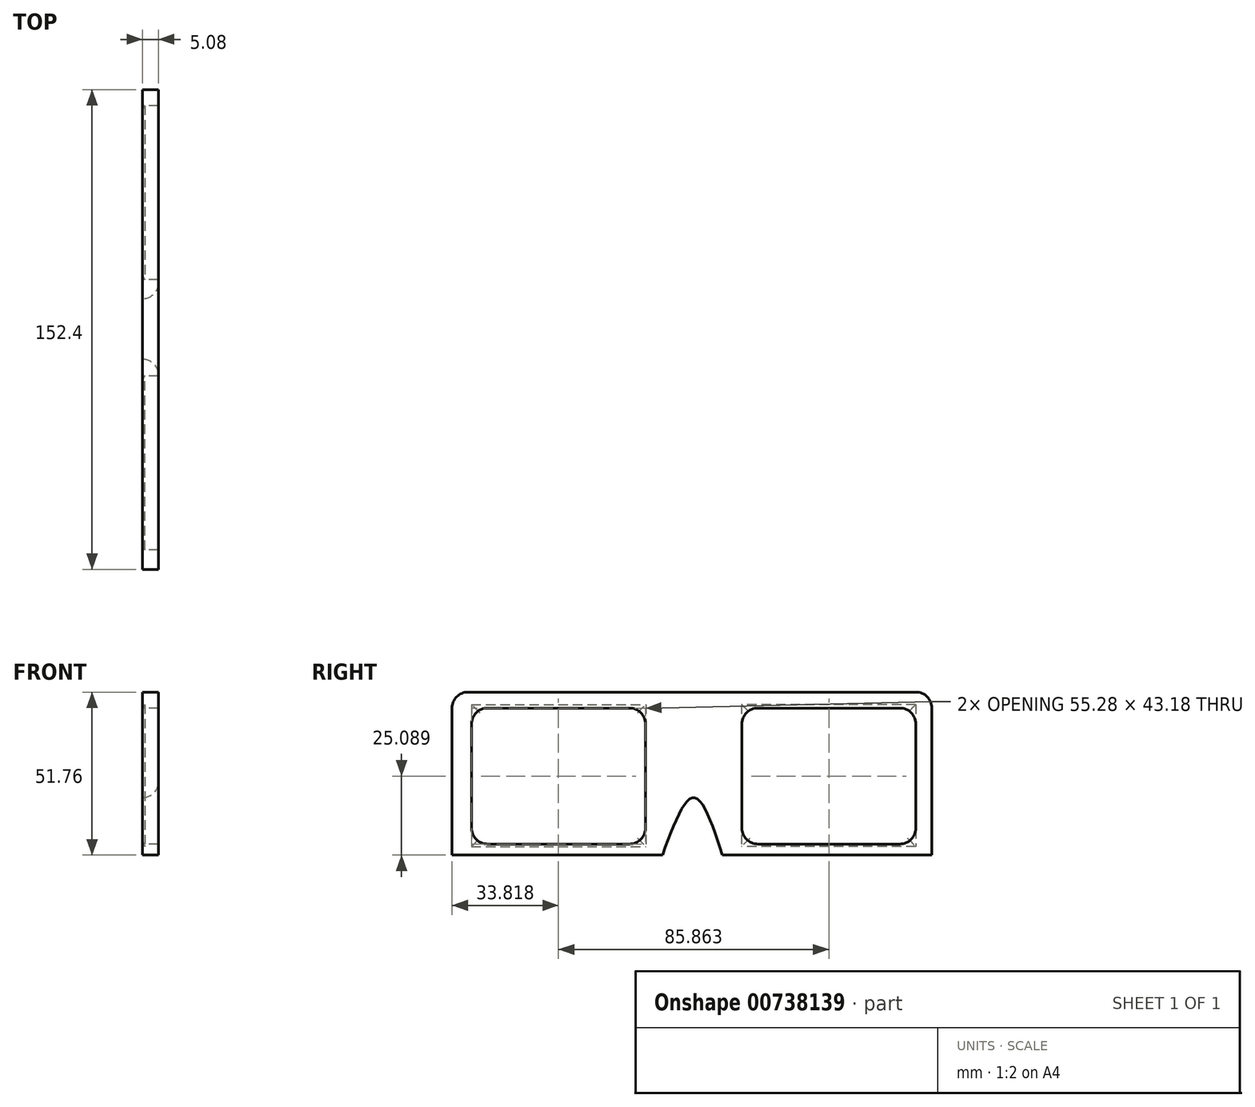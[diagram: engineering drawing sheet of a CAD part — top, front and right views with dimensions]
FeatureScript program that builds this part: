
annotation { "Feature Type Name" : "Feature", "Feature Type Description" : "" }
export const myFeature = defineFeature(function(context is Context, id is Id, definition is map)
    precondition{}
    {
        {
            var Q0;
            Q0=qCreatedBy(makeId("Right.planeOp"),FACE);
            var sketch = newSketch(context, id + "F0", { "sketchPlane" : qUnion([Q0])});
            skLineSegment(sketch, "E0.bottom", {"start": v(-76.75, 40.78) * mm, "end": v(75.65, 40.78) * mm});
            skLineSegment(sketch, "E0.top", {"start": v(-76.75, -22.72) * mm, "end": v(75.65, -22.72) * mm});
            skLineSegment(sketch, "E0.left", {"start": v(-76.75, 40.78) * mm, "end": v(-76.75, -22.72) * mm});
            skLineSegment(sketch, "E0.right", {"start": v(75.65, 40.78) * mm, "end": v(75.65, -22.72) * mm});
            skSolve(sketch);
        }
        {
            var Q0;
            Q0 = qSketchRegion(id + "F0", true);
            extrude(context, id + "F1", {"entities" : qUnion([Q0]), "depth" : 5.08 * mm, "offsetDistance" : 25.4 * mm});
        }
        {
            var Q0;
            Q0=makeQuery(id+"F1.opExtrude","SWEPT_EDGE",EDGE,{"disambiguationData":[OSD([sQuery(id+"F0.wireOp",EDGE,"E0.bottom"),sQuery(id+"F0.wireOp",EDGE,"E0.left")])]});
            var Q1;
            Q1=makeQuery(id+"F1.opExtrude","SWEPT_EDGE",EDGE,{"disambiguationData":[OSD([sQuery(id+"F0.wireOp",EDGE,"E0.top"),sQuery(id+"F0.wireOp",EDGE,"E0.left")])]});
            var Q2;
            Q2=makeQuery(id+"F1.opExtrude","SWEPT_EDGE",EDGE,{"disambiguationData":[OSD([sQuery(id+"F0.wireOp",EDGE,"E0.top"),sQuery(id+"F0.wireOp",EDGE,"E0.right")])]});
            var Q3;
            Q3=makeQuery(id+"F1.opExtrude","SWEPT_EDGE",EDGE,{"disambiguationData":[OSD([sQuery(id+"F0.wireOp",EDGE,"E0.bottom"),sQuery(id+"F0.wireOp",EDGE,"E0.right")])]});
            fillet(context, id + "F2", {"entities" : qUnion([Q0, Q1, Q2, Q3]), "radius" : 5.08 * mm, "tangentPropagation" : true, "allowEdgeOverflow" : false});
        }
        {
            var Q0;
            Q0=makeQuery(id+"F1.opExtrude","CAP_FACE",FACE,{"disambiguationData":[OSD([sQuery(id+"F0.wireOp",EDGE,"E0.bottom"),sQuery(id+"F0.wireOp",EDGE,"E0.top"),sQuery(id+"F0.wireOp",EDGE,"E0.left"),sQuery(id+"F0.wireOp",EDGE,"E0.right")])],"isStart":true});
            var sketch = newSketch(context, id + "F3", { "sketchPlane" : qUnion([Q0])});
            skLineSegment(sketch, "E1.bottom", {"start": v(-70.57, 35.7) * mm, "end": v(-15.3, 35.7) * mm});
            skLineSegment(sketch, "E1.top", {"start": v(-70.57, -7.48) * mm, "end": v(-15.3, -7.48) * mm});
            skLineSegment(sketch, "E1.left", {"start": v(-70.57, 35.7) * mm, "end": v(-70.57, -7.48) * mm});
            skLineSegment(sketch, "E1.right", {"start": v(-15.3, 35.7) * mm, "end": v(-15.3, -7.48) * mm});
            skLineSegment(sketch, "E2.MirrorCS", {"start": v(70.57, -7.48) * mm, "end": v(15.3, -7.48) * mm});
            skLineSegment(sketch, "E3.MirrorCS", {"start": v(70.57, 35.7) * mm, "end": v(70.57, -7.48) * mm});
            skLineSegment(sketch, "E4.MirrorCS", {"start": v(15.3, 35.7) * mm, "end": v(15.3, -7.48) * mm});
            skLineSegment(sketch, "E5.MirrorCS", {"start": v(70.57, 35.7) * mm, "end": v(15.3, 35.7) * mm});
            skLineSegment(sketch, "E6", {"start": v(-75.65, -10.98) * mm, "end": v(76.75, -10.98) * mm});
            skLineSegment(sketch, "E7", {"start": v(76.75, -10.98) * mm, "end": v(76.75, -28.42) * mm});
            skLineSegment(sketch, "E8", {"start": v(76.75, -28.42) * mm, "end": v(-75.65, -28.42) * mm});
            skLineSegment(sketch, "E9", {"start": v(-75.65, -28.42) * mm, "end": v(-75.65, -10.98) * mm});
            skFitSpline(sketch, "E10", {"points": [v(-9.1, -10.98) * mm, v(0, 7.25) * mm, v(9.9, -10.98) * mm], "startDerivative": vector(17.93, 54.77) * mm, "endDerivative": vector(20.06, -54.6) * mm});
            skSolve(sketch);
        }
        {
            var Q0;
            Q0 = qSketchRegion(id + "F3", true);
            extrude(context, id + "F4", {"entities" : qUnion([Q0]), "operationType" : NewBodyOperationType.REMOVE, "oppositeDirection" : true, "depth" : 25.4 * mm, "offsetDistance" : 25.4 * mm});
        }
        {
            var Q0;
            Q0=makeQuery(id+"F4.boolean.opBoolean","COPY",EDGE,{"derivedFrom":makeQuery(id+"F4.opExtrude","SWEPT_EDGE",EDGE,{"disambiguationData":[OSD([sQuery(id+"F0.wireOp",EDGE,"E0.right"),sQuery(id+"F3.wireOp",EDGE,"E6"),sQuery(id+"F3.wireOp",EDGE,"E9")])]})});
            var Q1;
            Q1=makeQuery(id+"F4.boolean.opBoolean","COPY",EDGE,{"derivedFrom":makeQuery(id+"F4.opExtrude","CAP_EDGE",EDGE,{"disambiguationData":[OSD([sQuery(id+"F3.wireOp",EDGE,"E10")])],"isStart":true})});
            var Q2;
            Q2=makeQuery(id+"F4.boolean.opBoolean","INTERSECT",EDGE,{"derivedFrom":[makeQuery(id+"F1.opExtrude","CAP_FACE",FACE,{"disambiguationData":[OSD([sQuery(id+"F0.wireOp",EDGE,"E0.bottom"),sQuery(id+"F0.wireOp",EDGE,"E0.top"),sQuery(id+"F0.wireOp",EDGE,"E0.left"),sQuery(id+"F0.wireOp",EDGE,"E0.right")])],"isStart":false}),makeQuery(id+"F4.opExtrude","SWEPT_FACE",FACE,{"disambiguationData":[OSD([sQuery(id+"F3.wireOp",EDGE,"E10")])]})]});
            var Q3;
            Q3=makeQuery(id+"F4.boolean.opBoolean","COPY",EDGE,{"derivedFrom":makeQuery(id+"F4.opExtrude","SWEPT_EDGE",EDGE,{"disambiguationData":[OSD([sQuery(id+"F0.wireOp",EDGE,"E0.left"),sQuery(id+"F3.wireOp",EDGE,"E6"),sQuery(id+"F3.wireOp",EDGE,"E7")])]})});
            var Q4;
            Q4=makeQuery(id+"F4.boolean.opBoolean","COPY",EDGE,{"derivedFrom":makeQuery(id+"F4.opExtrude","SWEPT_EDGE",EDGE,{"disambiguationData":[OSD([sQuery(id+"F3.wireOp",EDGE,"E3.MirrorCS"),sQuery(id+"F3.wireOp",EDGE,"E5.MirrorCS")])]})});
            var Q5;
            Q5=makeQuery(id+"F4.boolean.opBoolean","COPY",EDGE,{"derivedFrom":makeQuery(id+"F4.opExtrude","SWEPT_EDGE",EDGE,{"disambiguationData":[OSD([sQuery(id+"F3.wireOp",EDGE,"E4.MirrorCS"),sQuery(id+"F3.wireOp",EDGE,"E5.MirrorCS")])]})});
            var Q6;
            Q6=makeQuery(id+"F4.boolean.opBoolean","COPY",EDGE,{"derivedFrom":makeQuery(id+"F4.opExtrude","SWEPT_EDGE",EDGE,{"disambiguationData":[OSD([sQuery(id+"F3.wireOp",EDGE,"E2.MirrorCS"),sQuery(id+"F3.wireOp",EDGE,"E3.MirrorCS")])]})});
            var Q7;
            Q7=makeQuery(id+"F4.boolean.opBoolean","COPY",EDGE,{"derivedFrom":makeQuery(id+"F4.opExtrude","SWEPT_EDGE",EDGE,{"disambiguationData":[OSD([sQuery(id+"F3.wireOp",EDGE,"E2.MirrorCS"),sQuery(id+"F3.wireOp",EDGE,"E4.MirrorCS")])]})});
            var Q8;
            Q8=makeQuery(id+"F4.boolean.opBoolean","COPY",EDGE,{"derivedFrom":makeQuery(id+"F4.opExtrude","SWEPT_EDGE",EDGE,{"disambiguationData":[OSD([sQuery(id+"F3.wireOp",EDGE,"E1.top"),sQuery(id+"F3.wireOp",EDGE,"E1.left")])]})});
            var Q9;
            Q9=makeQuery(id+"F4.boolean.opBoolean","COPY",EDGE,{"derivedFrom":makeQuery(id+"F4.opExtrude","SWEPT_EDGE",EDGE,{"disambiguationData":[OSD([sQuery(id+"F3.wireOp",EDGE,"E1.top"),sQuery(id+"F3.wireOp",EDGE,"E1.right")])]})});
            var Q10;
            Q10=makeQuery(id+"F4.boolean.opBoolean","COPY",EDGE,{"derivedFrom":makeQuery(id+"F4.opExtrude","SWEPT_EDGE",EDGE,{"disambiguationData":[OSD([sQuery(id+"F3.wireOp",EDGE,"E1.bottom"),sQuery(id+"F3.wireOp",EDGE,"E1.right")])]})});
            var Q11;
            Q11=makeQuery(id+"F4.boolean.opBoolean","COPY",EDGE,{"derivedFrom":makeQuery(id+"F4.opExtrude","SWEPT_EDGE",EDGE,{"disambiguationData":[OSD([sQuery(id+"F3.wireOp",EDGE,"E1.bottom"),sQuery(id+"F3.wireOp",EDGE,"E1.left")])]})});
            fillet(context, id + "F5", {"entities" : qUnion([Q0, Q1, Q2, Q3, Q4, Q5, Q6, Q7, Q8, Q9, Q10, Q11]), "radius" : 5.08 * mm, "tangentPropagation" : true, "allowEdgeOverflow" : false});
        }
        {
            var Q0;
            Q0=qCreatedBy(makeId("Right.planeOp"),FACE);
            var sketch = newSketch(context, id + "F6", { "sketchPlane" : qUnion([Q0])});
            skLineSegment(sketch, "E11.bottom", {"start": v(70.56, 36.85) * mm, "end": v(15.22, 36.85) * mm});
            skLineSegment(sketch, "E11.top", {"start": v(70.56, -8.27) * mm, "end": v(15.22, -8.27) * mm});
            skLineSegment(sketch, "E11.left", {"start": v(70.56, 36.85) * mm, "end": v(70.56, -8.27) * mm});
            skLineSegment(sketch, "E11.right", {"start": v(15.22, 36.85) * mm, "end": v(15.22, -8.27) * mm});
            skLineSegment(sketch, "E12.MirrorCS", {"start": v(-15.22, 36.85) * mm, "end": v(-15.22, -8.27) * mm});
            skLineSegment(sketch, "E13.MirrorCS", {"start": v(-70.56, -8.27) * mm, "end": v(-15.22, -8.27) * mm});
            skLineSegment(sketch, "E14.MirrorCS", {"start": v(-70.56, 36.85) * mm, "end": v(-15.22, 36.85) * mm});
            skLineSegment(sketch, "E15.MirrorCS", {"start": v(-70.56, 36.85) * mm, "end": v(-70.56, -8.27) * mm});
            skSolve(sketch);
        }
        {
            var Q0;
            Q0 = qSketchRegion(id + "F6", true);
            extrude(context, id + "F7", {"entities" : qUnion([Q0]), "depth" : 0.76 * mm, "offsetDistance" : 25.4 * mm});
        }
        {
            var Q0;
            Q0=makeQuery(id+"F7.opExtrude","CAP_FACE",FACE,{"disambiguationData":[OSD([sQuery(id+"F6.wireOp",EDGE,"E11.bottom"),sQuery(id+"F6.wireOp",EDGE,"E11.top"),sQuery(id+"F6.wireOp",EDGE,"E11.left"),sQuery(id+"F6.wireOp",EDGE,"E11.right")])],"isStart":true});
            fillet(context, id + "F8", {"entities" : qUnion([Q0]), "radius" : 5.08 * mm, "tangentPropagation" : true, "allowEdgeOverflow" : false});
        }
        {
            var Q0;
            Q0=makeQuery(id+"F7.opExtrude","CAP_FACE",FACE,{"disambiguationData":[OSD([sQuery(id+"F6.wireOp",EDGE,"E12.MirrorCS"),sQuery(id+"F6.wireOp",EDGE,"E13.MirrorCS"),sQuery(id+"F6.wireOp",EDGE,"E14.MirrorCS"),sQuery(id+"F6.wireOp",EDGE,"E15.MirrorCS")])],"isStart":true});
            fillet(context, id + "F9", {"entities" : qUnion([Q0]), "radius" : 5.08 * mm, "tangentPropagation" : true, "allowEdgeOverflow" : false});
        }
    });
